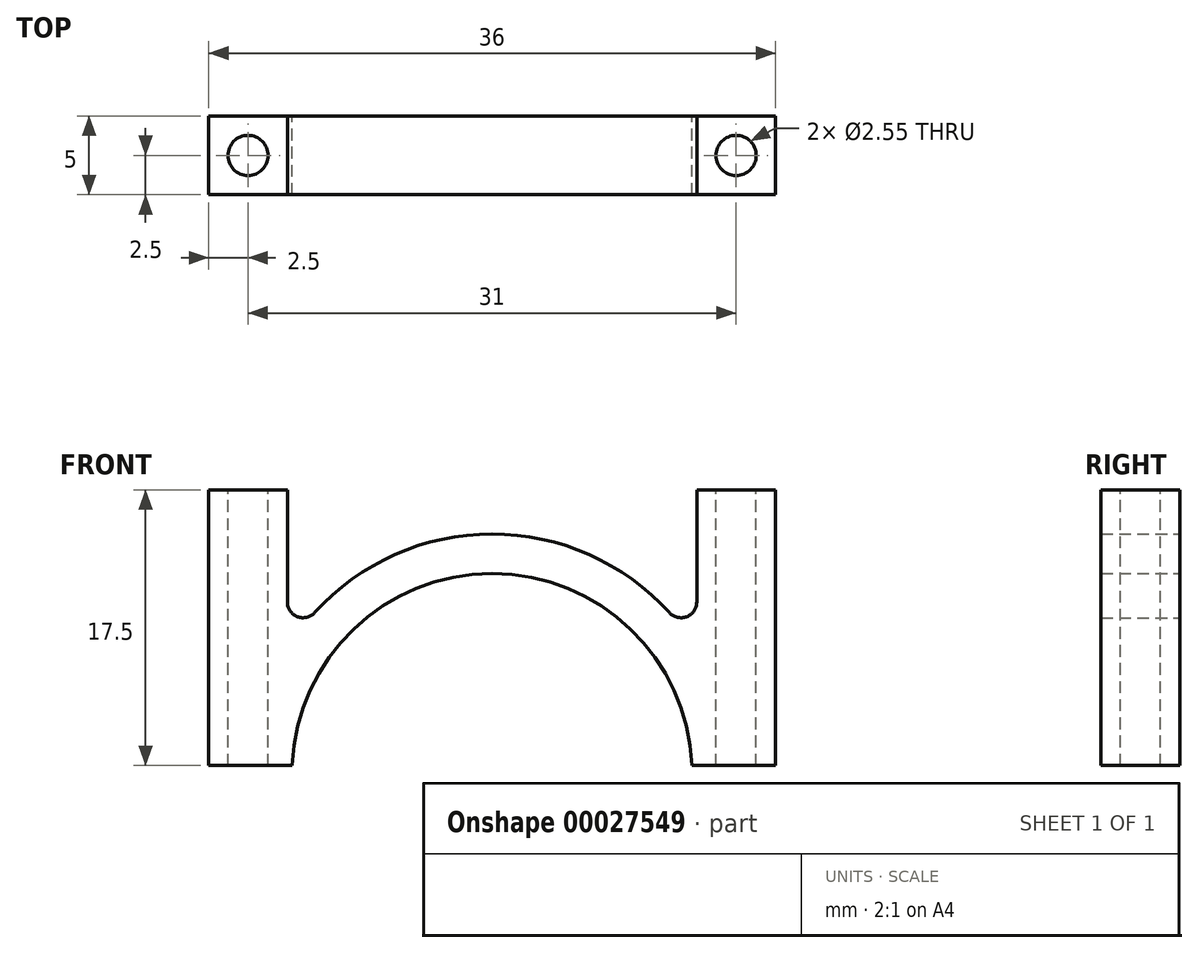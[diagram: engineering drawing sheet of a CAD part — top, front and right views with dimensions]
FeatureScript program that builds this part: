
annotation { "Feature Type Name" : "Feature", "Feature Type Description" : "" }
export const myFeature = defineFeature(function(context is Context, id is Id, definition is map)
    precondition{}
    {
        {
            var Q0;
            Q0=qCreatedBy(makeId("Front.planeOp"),FACE);
            var sketch = newSketch(context, id + "F0", { "sketchPlane" : qUnion([Q0])});
            skLineSegment(sketch, "E0", {"start": v(-20.64, 0) * mm, "end": v(20.64, 0) * mm, "construction": true});
            skArc(sketch, "E1", {"start": v(12.7, 0.5) * mm, "mid": v(0, 12.7) * mm, "end": v(-12.7, 0.5) * mm});
            skLineSegment(sketch, "E2", {"start": v(0, 0) * mm, "end": v(0, 15.98) * mm, "construction": true});
            skArc(sketch, "E3.0", {"start": v(11.26, 10.21) * mm, "mid": v(0, 15.2) * mm, "end": v(-11.26, 10.21) * mm});
            skLineSegment(sketch, "E4.0", {"start": v(18, 0.5) * mm, "end": v(18, 18) * mm});
            skLineSegment(sketch, "E5.0", {"start": v(-18, 0.5) * mm, "end": v(-18, 18) * mm});
            skLineSegment(sketch, "E6", {"start": v(-18, 0.5) * mm, "end": v(-12.7, 0.5) * mm});
            skLineSegment(sketch, "E7.0", {"start": v(-13, 10.88) * mm, "end": v(-13, 18) * mm});
            skLineSegment(sketch, "E8.0", {"start": v(13, 10.88) * mm, "end": v(13, 18) * mm});
            skLineSegment(sketch, "E9", {"start": v(-18, 18) * mm, "end": v(-13, 18) * mm});
            skLineSegment(sketch, "E10", {"start": v(13, 18) * mm, "end": v(18, 18) * mm});
            skLineSegment(sketch, "E11.trimOffspring", {"start": v(12.7, 0.5) * mm, "end": v(18, 0.5) * mm});
            skPoint(sketch, "E12.visualSharp", {"position": v(-13, 7.88) * mm});
            skArc(sketch, "E12.filletArc", {"start": v(-13, 10.88) * mm, "mid": v(-12.36, 9.95) * mm, "end": v(-11.26, 10.21) * mm});
            skPoint(sketch, "E13.visualSharp", {"position": v(13, 7.88) * mm});
            skArc(sketch, "E13.filletArc", {"start": v(11.26, 10.21) * mm, "mid": v(12.36, 9.95) * mm, "end": v(13, 10.88) * mm});
            skSolve(sketch);
        }
        {
            var Q0;
            Q0 = qSketchRegion(id + "F0", true);
            extrude(context, id + "F1", {"entities" : qUnion([Q0]), "depth" : 5 * mm});
        }
        {
            var Q0;
            Q0=makeQuery(id+"F1.opExtrude","SWEPT_FACE",FACE,{"disambiguationData":[OSD([sQuery(id+"F0.wireOp",EDGE,"E9")])]});
            var sketch = newSketch(context, id + "F2", { "sketchPlane" : qUnion([Q0])});
            skPoint(sketch, "E14", {"position": v(-15.5, -2.5) * mm});
            skPoint(sketch, "E14.positionSnap0", {"position": v(-15.5, 0) * mm});
            skPoint(sketch, "E14.positionSnap1", {"position": v(-18, -2.5) * mm});
            skPoint(sketch, "E15.MirrorP", {"position": v(15.5, -2.5) * mm});
            skSolve(sketch);
        }
        {
            var Q0;
            Q0=sQuery(id+"F2.wireOp",VERTEX,"E14");
            var Q1;
            Q1=sQuery(id+"F2.wireOp",VERTEX,"E15.MirrorP");
            var Q2;
            Q2=makeQuery(id+"F1.opExtrude","SWEPT_BODY",BODY,{"disambiguationData":[OSD([sQuery(id+"F0.wireOp",EDGE,"E1"),sQuery(id+"F0.wireOp",EDGE,"E3.0"),sQuery(id+"F0.wireOp",EDGE,"E4.0"),sQuery(id+"F0.wireOp",EDGE,"E5.0"),sQuery(id+"F0.wireOp",EDGE,"E6"),sQuery(id+"F0.wireOp",EDGE,"E7.0"),sQuery(id+"F0.wireOp",EDGE,"E8.0"),sQuery(id+"F0.wireOp",EDGE,"E9"),sQuery(id+"F0.wireOp",EDGE,"E10"),sQuery(id+"F0.wireOp",EDGE,"E11.trimOffspring"),sQuery(id+"F0.wireOp",EDGE,"E12.filletArc"),sQuery(id+"F0.wireOp",EDGE,"E13.filletArc")])]});
            hole(context, id + "F3", {"style" : HoleStyle.SIMPLE, "holeDiameter" : 2.55 * mm, "endStyle" : HoleEndStyle.THROUGH, "locations" : qUnion([Q0, Q1]), "scope" : qUnion([Q2])});
        }
    });
